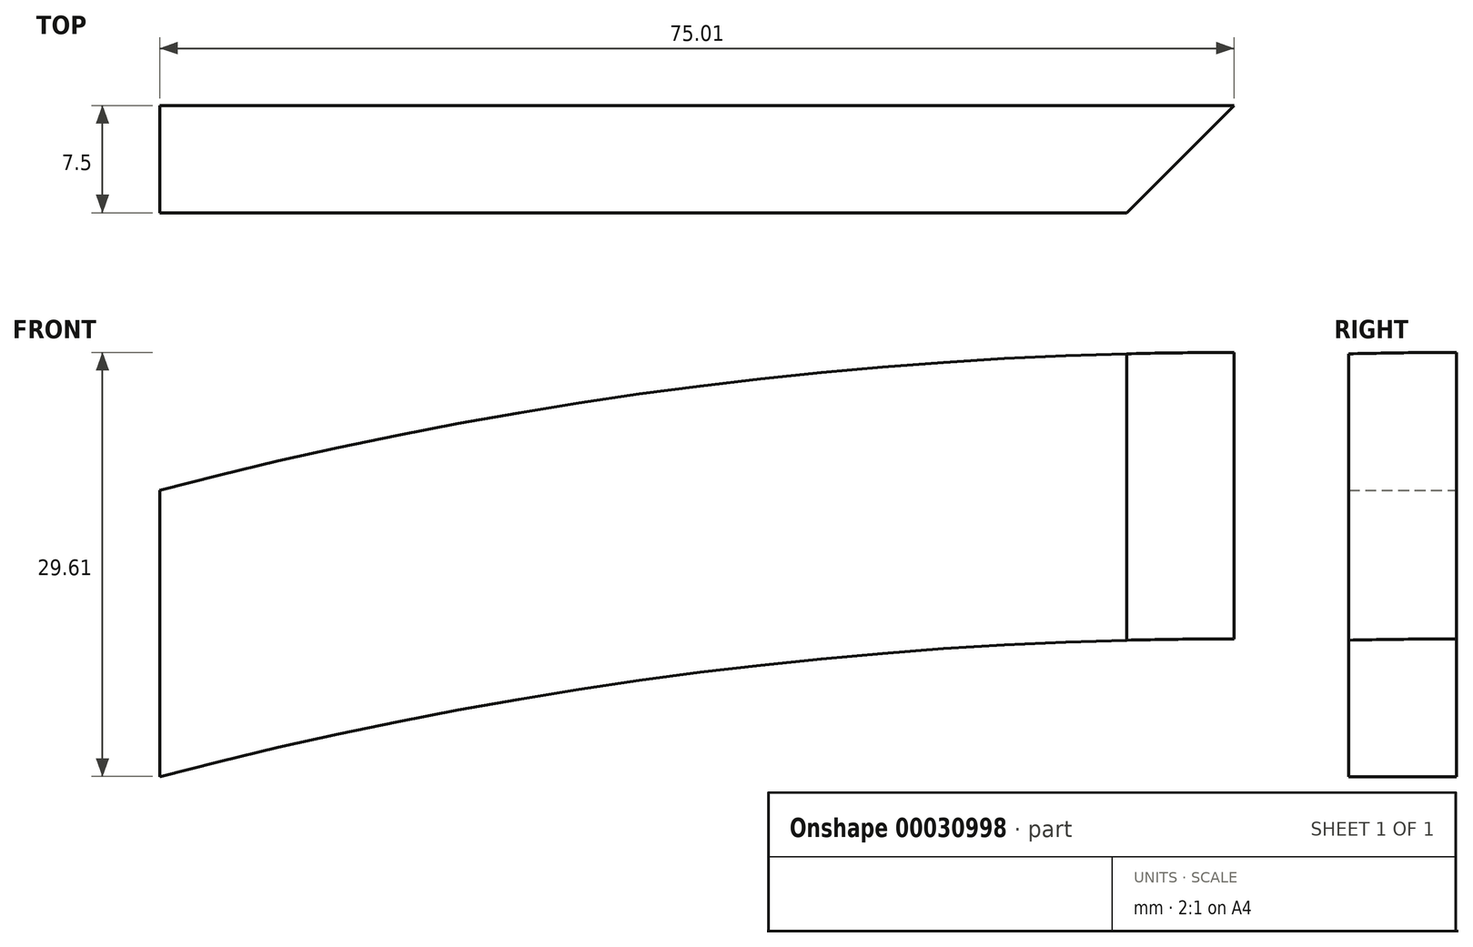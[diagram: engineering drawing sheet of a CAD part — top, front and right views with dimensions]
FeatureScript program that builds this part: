
annotation { "Feature Type Name" : "Feature", "Feature Type Description" : "" }
export const myFeature = defineFeature(function(context is Context, id is Id, definition is map)
    precondition{}
    {
        {
            var Q0;
            Q0=qCreatedBy(makeId("Front.planeOp"),FACE);
            var sketch = newSketch(context, id + "F0", { "sketchPlane" : qUnion([Q0])});
            skLineSegment(sketch, "E0", {"start": v(-86.74, -6.41) * mm, "end": v(-86.74, 13.59) * mm});
            skArc(sketch, "E1", {"start": v(-11.73, 23.2) * mm, "mid": v(-49.54, 20.8) * mm, "end": v(-86.74, 13.59) * mm});
            skArc(sketch, "E2", {"start": v(-11.73, 3.2) * mm, "mid": v(-49.54, 0.8) * mm, "end": v(-86.74, -6.41) * mm});
            skLineSegment(sketch, "E3", {"start": v(-11.73, 23.2) * mm, "end": v(-11.73, 3.2) * mm});
            skSolve(sketch);
        }
        {
            var Q0;
            Q0=makeQuery(id+"F0.imprint","IMPRINT",FACE,{"disambiguationData":[TD([[makeQuery(id+"F0.imprint","IMPRINT",EDGE,{"derivedFrom":sQuery(id+"F0.wireOp",EDGE,"E0")}),-1.0]])]});
            extrude(context, id + "F1", {"entities" : qUnion([Q0]), "depth" : 7.5 * mm});
        }
        {
            var Q0;
            Q0=makeQuery(id+"F1.opExtrude","CAP_EDGE",EDGE,{"disambiguationData":[OSD([sQuery(id+"F0.wireOp",EDGE,"E3")])],"isStart":false});
            chamfer(context, id + "F2", {"entities" : qUnion([Q0]), "width" : 7.5 * mm, "tangentPropagation" : true});
        }
    });
